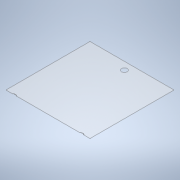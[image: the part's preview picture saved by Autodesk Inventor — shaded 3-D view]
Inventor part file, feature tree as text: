
AUTODESK INVENTOR PART (.ipt)
format: ipt  version: 2022 (Build 260153000, 153)  size: 144,384 bytes
history: native  units: mm
features: sketch x4, extrude x2, hole x2, other x1, fillet x1
ambient origin geometry x8: Origin, YZ Plane, XZ Plane, XY Plane, X Axis, Y Axis, Z Axis, Center Point
bodies: Body1 (feature_tree)
feature tree (10):
  other  "Sólido1"
  extrude  "Extrusão1"  Depth=440.0mm
  hole  "Furo1"  [1 undecoded]
  fillet  "Arredondamento1"  Radius=18.0mm
  hole  "Furo2"  [1 undecoded]
  extrude  "Extrusão2"  Depth=18.0mm
  sketch  "Esboço1"  dims[d0=440.0mm d1=440.0mm]
  sketch  "Esboço2"  dims[d2=2.0mm d3=0.0mm]
  sketch  "Esboço3"  dims[d4=2.0mm d5=6.0mm d6=4.0mm d7=2.0mm d8=90.0deg d9=8.0mm d10=20.594885mm d11=2.0mm]
  sketch  "Esboço4"  dims[d12=30.0mm d13=6.0mm d14=4.0mm d15=2.0mm d16=90.0deg d17=8.0mm d18=20.594885mm d19=18.0mm d20=3.0mm d21=18.0mm d22=3.0mm d23=2.0mm d24=0.0mm]
note: 2 required parameter values undecoded (feature->parameter linkage not recoverable at this tier; creation-order binding heuristic only, values carry confidence <= 0.55)
